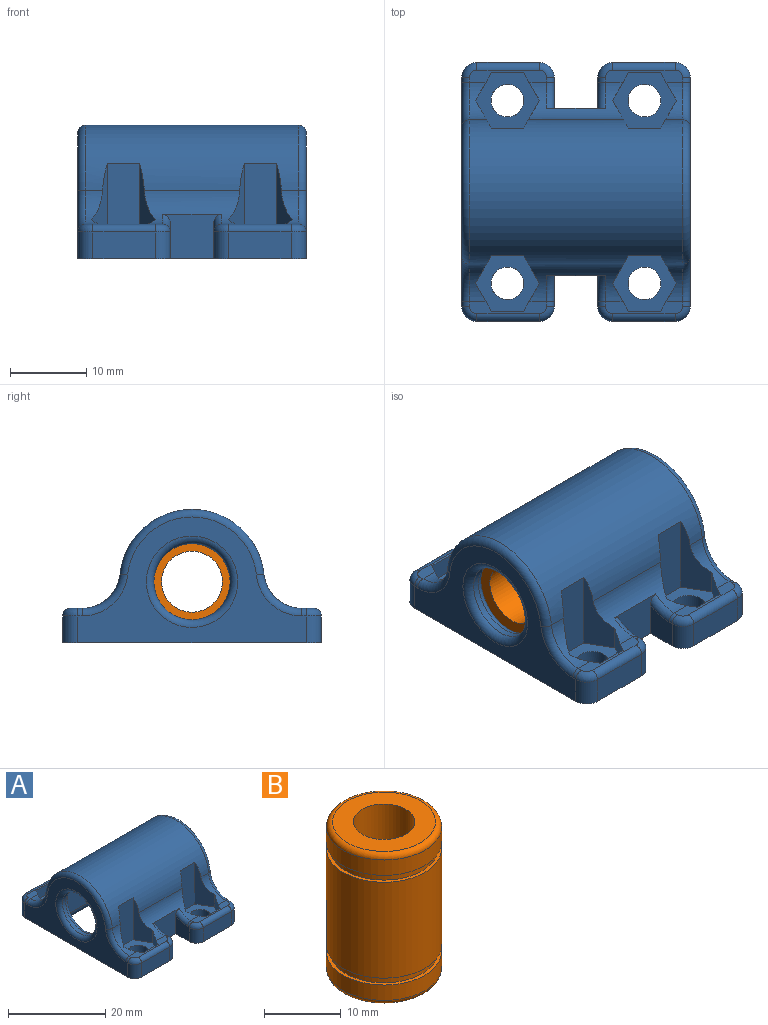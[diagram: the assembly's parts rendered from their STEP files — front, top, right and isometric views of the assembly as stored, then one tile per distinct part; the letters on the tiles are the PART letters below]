
ASSEMBLY  parts=2 mates=1
PART A: 114 faces, bbox 30.4x34.4x18.3 mm
  f0: cylinder r=2.15mm len=4.3mm, axis (0,0,-1), area 27mm2, adj f21,f94
  f1: cylinder r=2.15mm len=4.3mm, axis (0,0,-1), area 27mm2, adj f21,f95
  f2: cylinder r=2.15mm len=4.3mm, axis (0,0,-1), area 27mm2, adj f21,f108
  f3: cylinder r=2.15mm len=4.3mm, axis (0,0,-1), area 27mm2, adj f21,f81
  f4: cylinder r=5mm len=4.97mm, axis (-1,0,0), area 11.9mm2, adj f20,f22,f55,f103,f104
  f5: cylinder r=5mm len=4.97mm, axis (-1,0,0), area 11.9mm2, adj f9,f22,f70,f97,f98
  f6: cylinder r=5mm len=4.97mm, axis (-1,0,0), area 11.9mm2, adj f16,f22,f68,f89,f90
  f7: cylinder r=5mm len=4.97mm, axis (-1,0,0), area 11.9mm2, adj f8,f22,f53,f83,f84
  f8: plane 10.15x1.58mm, normal (0,0,1), area 9.5mm2, adj f7,f46,f48,f49,f50,f51,f52,f84
  f9: plane 10.15x1.58mm, normal (0,0,1), area 9.5mm2, adj f5,f45,f71,f72,f73,f74,f75,f98
  f10: plane 8.15x3.5mm, normal (0,-1,0), area 28.5mm2, adj f21,f33,f42,f73
  f11: plane 8.15x3.5mm, normal (0,1,0), area 28.5mm2, adj f21,f36,f43,f65
  f12: plane 24.2x6mm, normal (0,1,0), area 145.2mm2, adj f14,f24,f26,f39
  f13: plane 24.2x6mm, normal (0,-1,0), area 145.2mm2, adj f14,f24,f26,f38
  f14: cylinder r=7.55mm len=24.2mm, axis (-1,0,0), area 446.8mm2, adj f12,f13,f24,f26,f109,f110,f112,f113
  f15: plane 30x16.5mm, normal (-1,0,0), area 196.5mm2, adj f21,f41,f44,f52,f53,f54,f55,f56
  f16: plane 10.15x1.58mm, normal (0,0,1), area 9.5mm2, adj f6,f46,f63,f64,f65,f66,f67,f90
  f17: plane 8.15x3.5mm, normal (0,-1,0), area 28.5mm2, adj f21,f34,f41,f58
  f18: plane 30x16.5mm, normal (1,0,0), area 196.5mm2, adj f21,f42,f43,f67,f68,f69,f70,f71
  f19: plane 8.15x3.5mm, normal (0,1,0), area 28.5mm2, adj f21,f35,f44,f50
  f20: plane 10.15x1.58mm, normal (0,0,1), area 9.5mm2, adj f4,f45,f56,f57,f58,f59,f60,f104
  f21: plane 34x30mm, normal (0,0,-1), area 348mm2, adj f0,f1,f2,f3,f10,f11,f15,f17
  f22: cylinder r=9.5mm len=28mm, axis (-1,0,0), area 706mm2, adj f4,f5,f6,f7,f45,f46,f54,f69
  f23: cylinder r=5mm len=10mm, axis (-1,0,0), area 28.3mm2, adj f79,f80
  f24: plane 15.1x13.55mm, normal (1,0,0), area 67mm2, adj f12,f13,f14,f37,f80
  f25: cylinder r=5mm len=10mm, axis (1,0,0), area 28.3mm2, adj f77,f78
  f26: plane 15.1x13.55mm, normal (-1,0,0), area 67mm2, adj f12,f13,f14,f40,f77
  f27: plane 4.57x4mm, normal (-1,0,0), area 15.2mm2, adj f21,f28,f33,f75,f76
  f28: plane 7.7x5.85mm, normal (0,-1,0), area 33.9mm2, adj f21,f27,f29,f45,f61,f76
  f29: plane 4.57x4mm, normal (1,0,0), area 15.2mm2, adj f21,f28,f34,f60,f61
  f30: plane 4.57x4mm, normal (1,0,0), area 15.2mm2, adj f21,f31,f35,f47,f48
  f31: plane 7.7x5.85mm, normal (0,1,0), area 33.9mm2, adj f21,f30,f32,f46,f47,f62
  f32: plane 4.57x4mm, normal (-1,0,0), area 15.2mm2, adj f21,f31,f36,f62,f63
  f33: cylinder r=2mm len=3.5mm, axis (0,0,1), area 11mm2, adj f10,f21,f27,f74
  f34: cylinder r=2mm len=3.5mm, axis (0,0,-1), area 11mm2, adj f17,f21,f29,f59
  f35: cylinder r=2mm len=3.5mm, axis (0,0,-1), area 11mm2, adj f19,f21,f30,f49
  f36: cylinder r=2mm len=3.5mm, axis (0,0,1), area 11mm2, adj f11,f21,f32,f64
  f37: cylinder r=2mm len=19.1mm, axis (0,-1,0), area 52mm2, adj f21,f24,f38,f39
  f38: cylinder r=2mm len=28.2mm, axis (-1,0,0), area 80.6mm2, adj f13,f21,f37,f40
  f39: cylinder r=2mm len=28.2mm, axis (1,0,0), area 80.6mm2, adj f12,f21,f37,f40
  f40: cylinder r=2mm len=19.1mm, axis (0,-1,0), area 52mm2, adj f21,f26,f38,f39
  f41: cylinder r=2mm len=3.5mm, axis (0,0,-1), area 11mm2, adj f15,f17,f21,f57
  f42: cylinder r=2mm len=3.5mm, axis (0,0,1), area 11mm2, adj f10,f18,f21,f72
  f43: cylinder r=2mm len=3.5mm, axis (0,0,-1), area 11mm2, adj f11,f18,f21,f66
  f44: cylinder r=2mm len=3.5mm, axis (0,0,1), area 11mm2, adj f15,f19,f21,f51
  f45: cylinder r=5mm len=12.52mm, axis (-1,0,0), area 53.5mm2, adj f9,f20,f22,f28,f61,f76,f100,f101
  f46: cylinder r=5mm len=12.52mm, axis (-1,0,0), area 53.5mm2, adj f8,f16,f22,f31,f47,f62,f86,f87
  f47: torus R=6mm, axis (-1,0,0), area 5.8mm2, adj f30,f31,f46,f48
  f48: cylinder r=1mm len=1mm, axis (0,1,0), area 0.9mm2, adj f8,f30,f47,f49
  f49: torus R=1mm, axis (0,0,1), area 4mm2, adj f8,f35,f48,f50
  f50: cylinder r=1mm len=8.15mm, axis (1,0,0), area 12.8mm2, adj f8,f19,f49,f51
  f51: torus R=1mm, axis (0,0,1), area 4mm2, adj f8,f44,f50,f52
  f52: cylinder r=1mm len=1mm, axis (0,1,0), area 0.9mm2, adj f8,f15,f51,f53
  f53: torus R=6mm, axis (1,0,0), area 12.4mm2, adj f7,f15,f52,f54
  f54: torus R=8.5mm, axis (1,0,0), area 42.1mm2, adj f15,f22,f53,f55
  f55: torus R=6mm, axis (1,0,0), area 12.4mm2, adj f4,f15,f54,f56
  f56: cylinder r=1mm len=1mm, axis (0,1,0), area 0.9mm2, adj f15,f20,f55,f57
  f57: torus R=1mm, axis (0,0,1), area 4mm2, adj f20,f41,f56,f58
  f58: cylinder r=1mm len=8.15mm, axis (-1,0,0), area 12.8mm2, adj f17,f20,f57,f59
  f59: torus R=1mm, axis (0,0,1), area 4mm2, adj f20,f34,f58,f60
  f60: cylinder r=1mm len=1mm, axis (0,1,0), area 0.9mm2, adj f20,f29,f59,f61
  f61: torus R=6mm, axis (1,0,0), area 5.8mm2, adj f28,f29,f45,f60
  f62: torus R=6mm, axis (-1,0,0), area 5.8mm2, adj f31,f32,f46,f63
  f63: cylinder r=1mm len=1mm, axis (0,-1,0), area 0.9mm2, adj f16,f32,f62,f64
  f64: torus R=1mm, axis (0,0,1), area 4mm2, adj f16,f36,f63,f65
  f65: cylinder r=1mm len=8.15mm, axis (1,0,0), area 12.8mm2, adj f11,f16,f64,f66
  f66: torus R=1mm, axis (0,0,1), area 4mm2, adj f16,f43,f65,f67
  f67: cylinder r=1mm len=1mm, axis (0,-1,0), area 0.9mm2, adj f16,f18,f66,f68
  f68: torus R=6mm, axis (1,0,0), area 12.4mm2, adj f6,f18,f67,f69
  f69: torus R=8.5mm, axis (1,0,0), area 42.1mm2, adj f18,f22,f68,f70
  f70: torus R=6mm, axis (1,0,0), area 12.4mm2, adj f5,f18,f69,f71
  f71: cylinder r=1mm len=1mm, axis (0,-1,0), area 0.9mm2, adj f9,f18,f70,f72
  f72: torus R=1mm, axis (0,0,1), area 4mm2, adj f9,f42,f71,f73
  f73: cylinder r=1mm len=8.15mm, axis (-1,0,0), area 12.8mm2, adj f9,f10,f72,f74
  f74: torus R=1mm, axis (0,0,1), area 4mm2, adj f9,f33,f73,f75
  f75: cylinder r=1mm len=1mm, axis (0,-1,0), area 0.9mm2, adj f9,f27,f74,f76
  f76: torus R=6mm, axis (1,0,0), area 5.8mm2, adj f27,f28,f45,f75
  f77: torus R=6mm, axis (1,0,0), area 52.9mm2, adj f25,f26
  f78: torus R=6mm, axis (1,0,0), area 52.9mm2, adj f18,f25
  f79: torus R=6mm, axis (1,0,0), area 52.9mm2, adj f15,f23
  f80: torus R=6mm, axis (-1,0,0), area 52.9mm2, adj f23,f24
  f81: plane 8.43x7.3mm, normal (0,0,1), area 31.6mm2, adj f3,f82,f83,f84,f85,f86,f87
  f82: plane 10.53x4.21mm, normal (0,1,0), area 44.4mm2, adj f22,f81,f83,f87
  f83: plane 10.53x3.65mm, normal (0.87,0.5,0), area 24.5mm2, adj f7,f22,f81,f82,f84
  f84: plane 3.7x3.17mm, normal (0.87,-0.5,0), area 11.1mm2, adj f7,f8,f81,f83,f85
  f85: plane 4.21x2.5mm, normal (0,-1,0), area 10.5mm2, adj f8,f81,f84,f86
  f86: plane 3.7x3.17mm, normal (-0.87,-0.5,0), area 11.1mm2, adj f8,f46,f81,f85,f87
  f87: plane 10.53x3.65mm, normal (-0.87,0.5,0), area 24.5mm2, adj f22,f46,f81,f82,f86
  f88: plane 10.53x4.21mm, normal (0,1,0), area 44.4mm2, adj f22,f89,f93,f94
  f89: plane 10.53x3.65mm, normal (-0.87,0.5,0), area 24.5mm2, adj f6,f22,f88,f90,f94
  f90: plane 3.7x3.17mm, normal (-0.87,-0.5,0), area 11.1mm2, adj f6,f16,f89,f91,f94
  f91: plane 4.21x2.5mm, normal (0,-1,0), area 10.5mm2, adj f16,f90,f92,f94
  f92: plane 3.7x3.17mm, normal (0.87,-0.5,0), area 11.1mm2, adj f16,f46,f91,f93,f94
  f93: plane 10.53x3.65mm, normal (0.87,0.5,0), area 24.5mm2, adj f22,f46,f88,f92,f94
  f94: plane 8.43x7.3mm, normal (0,0,1), area 31.6mm2, adj f0,f88,f89,f90,f91,f92,f93
  f95: plane 8.43x7.3mm, normal (0,0,1), area 31.6mm2, adj f1,f96,f97,f98,f99,f100,f101
  f96: plane 10.53x4.21mm, normal (0,-1,0), area 44.4mm2, adj f22,f95,f97,f101
  f97: plane 10.53x3.65mm, normal (-0.87,-0.5,0), area 24.5mm2, adj f5,f22,f95,f96,f98
  f98: plane 3.7x3.17mm, normal (-0.87,0.5,0), area 11.1mm2, adj f5,f9,f95,f97,f99
  f99: plane 4.21x2.5mm, normal (0,1,0), area 10.5mm2, adj f9,f95,f98,f100
  f100: plane 3.7x3.17mm, normal (0.87,0.5,0), area 11.1mm2, adj f9,f45,f95,f99,f101
  f101: plane 10.53x3.65mm, normal (0.87,-0.5,0), area 24.5mm2, adj f22,f45,f95,f96,f100
  f102: plane 10.53x4.21mm, normal (0,-1,0), area 44.4mm2, adj f22,f103,f107,f108
  f103: plane 10.53x3.65mm, normal (0.87,-0.5,0), area 24.5mm2, adj f4,f22,f102,f104,f108
  f104: plane 3.7x3.17mm, normal (0.87,0.5,0), area 11.1mm2, adj f4,f20,f103,f105,f108
  f105: plane 4.21x2.5mm, normal (0,1,0), area 10.5mm2, adj f20,f104,f106,f108
  f106: plane 3.7x3.17mm, normal (-0.87,0.5,0), area 11.1mm2, adj f20,f45,f105,f107,f108
  f107: plane 10.53x3.65mm, normal (-0.87,-0.5,0), area 24.5mm2, adj f22,f45,f102,f106,f108
  f108: plane 8.43x7.3mm, normal (0,0,1), area 31.6mm2, adj f2,f102,f103,f104,f105,f106,f107
  f109: plane 5.64x1mm, normal (1,0,0), area 2.9mm2, adj f14,f111,f112,f113
  f110: plane 5.64x1mm, normal (-1,0,0), area 2.9mm2, adj f14,f111,f112,f113
  f111: plane 22x4.3mm, normal (0,0,-1), area 94.5mm2, adj f109,f110,f112,f113
  f112: plane 22x1mm, normal (0,-0.83,-0.56), area 26.5mm2, adj f14,f109,f110,f111
  f113: plane 22x1mm, normal (0,0.83,-0.56), area 26.5mm2, adj f14,f109,f110,f111
PART B: 14 faces, bbox 16.2x16.2x24 mm
  f0: cylinder r=7.5mm len=15mm, axis (0,0,-1), area 115.5mm2, adj f5,f12
  f1: cylinder r=4mm len=24mm, axis (0,0,-1), area 603.2mm2, adj f3,f4
  f2: cylinder r=7.5mm len=15mm, axis (0,0,-1), area 115.5mm2, adj f9,f13
  f3: plane 13.4x13.4mm, normal (0,0,1), area 90.8mm2, adj f1,f13
  f4: plane 13.4x13.4mm, normal (0,0,-1), area 90.8mm2, adj f1,f12
  f5: plane 15x15mm, normal (0,0,1), area 22.8mm2, adj f0,f6
  f6: cylinder r=7mm len=14mm, axis (0,0,1), area 48.4mm2, adj f5,f7
  f7: plane 15x15mm, normal (0,0,-1), area 22.8mm2, adj f6,f8
  f8: cylinder r=7.5mm len=15.3mm, axis (0,0,-1), area 721mm2, adj f7,f10
  f9: plane 15x15mm, normal (0,0,-1), area 22.8mm2, adj f2,f11
  f10: plane 15x15mm, normal (0,0,1), area 22.8mm2, adj f8,f11
  f11: cylinder r=7mm len=14mm, axis (0,0,1), area 48.4mm2, adj f9,f10
  f12: torus R=6.7mm, axis (0,0,1), area 56.9mm2, adj f0,f4
  f13: torus R=6.7mm, axis (0,0,1), area 56.9mm2, adj f2,f3
PLACE A t=(0,0,-2.5)mm
PLACE B rot(axis=(0,1,0),90deg) t=(-12,0,5.5)mm
MATE fastened B.f0 <-> A.f23  axis (-1,0,0) through (0,0,5.5)mm
